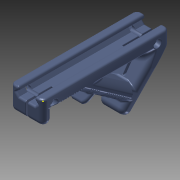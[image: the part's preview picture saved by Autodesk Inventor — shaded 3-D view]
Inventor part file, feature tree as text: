
AUTODESK INVENTOR PART (.ipt)
format: ipt  version: 2015 (Build 190159000, 159)  size: 5,217,280 bytes
history: native  units: mm
features: extrude x21, sketch x21, projected_geometry x20, fillet x18, plane x5, other x2, chamfer x2
ambient origin geometry x8: Origin, YZ Plane, XZ Plane, XY Plane, X Axis, Y Axis, Z Axis, Center Point
bodies: Solid1 (feature_tree)
feature tree (89):
  extrude  "Extrusion1"  Depth=35.0mm
  extrude  "Extrusion2"  Depth=10.0mm
  extrude  "Extrusion3"  Depth=12.0mm
  other  "Work Axis2"
  other  "Work Point2"
  plane  "Work Plane2"
  extrude  "Extrusion5"  Depth=12.0mm
  sketch  "Sketch9"  dims[d14=15.0mm d15=10.0mm d16=15.0mm d17=0.0mm]
  extrude  "Extrusion4"  TaperAngle=90.0deg  [1 undecoded]
  plane  "Work Plane3"
  plane  "Work Plane5"
  extrude  "Extrusion8"  Depth=10.0mm
  fillet  "Fillet3"  Radius=15.0mm
  extrude  "Extrusion9"  Depth=10.0mm
  fillet  "Fillet5"  Radius=130.0mm
  fillet  "Fillet6"  Radius=35.531179mm
  fillet  "Fillet7"  Radius=18.5mm
  fillet  "Fillet8"  Radius=18.5mm
  fillet  "Fillet9"  Radius=7.5mm
  extrude  "Extrusion10"  Depth=36.0mm TaperAngle=0.0deg
  fillet  "Fillet10"  Radius=35.75mm
  fillet  "Fillet11"  [1 undecoded]
  fillet  "Fillet12"  Radius=34.0mm
  plane  "Work Plane4"
  extrude  "Extrusion11"  Depth=5.0mm
  extrude  "Extrusion12"  Depth=13.5mm TaperAngle=0.0deg
  extrude  "Extrusion13"  Depth=5.0mm
  fillet  "Fillet13"  Radius=2.0mm
  fillet  "Fillet14"  Radius=2.0mm
  fillet  "Fillet15"  Radius=2.0mm
  extrude  "Extrusion14"  Depth=9.0mm
  extrude  "Extrusion15"  Depth=8.5mm
  extrude  "Extrusion16"  Depth=3.0mm
  fillet  "Fillet16"  [1 undecoded]
  extrude  "Extrusion17"  Depth=2.0mm
  extrude  "Extrusion18"  Depth=1.0mm
  plane  "Work Plane6"
  extrude  "Extrusion19"  Depth=110.0mm
  sketch  "Sketch27"  dims[d125=2.0mm d128=13.5mm d129=0.0mm]
  extrude  "Extrusion21"  Depth=13.5mm TaperAngle=0.0deg
  extrude  "Extrusion22"  Depth=5.0mm
  fillet  "Fillet17"  Radius=2.0mm
  fillet  "Fillet18"  Radius=8.0mm
  fillet  "Fillet19"  Radius=8.0mm
  extrude  "Extrusion23"  Depth=4.25mm
  extrude  "Extrusion24"  Depth=1.5mm
  fillet  "Fillet20"  Radius=0.5mm
  chamfer  "Chamfer3"  Distance=0.5mm
  chamfer  "Chamfer4"  Distance=25.0mm
  fillet  "Fillet22"  Radius=1.0mm
  sketch  "Sketch1"  dims[d0=135.0mm d1=35.0mm]
  sketch  "Sketch2"  dims[d2=10.0mm d3=0.0mm d4=10.0mm]
  projected_geometry  "Projected Loop1"
  sketch  "Sketch3"  dims[d5=15.0mm d6=0.0mm d7=12.0mm]
  projected_geometry  "Projected Loop2"
  sketch  "Sketch4"  dims[d10=9.599311mm d11=12.0mm]
  projected_geometry  "Projected Loop3"
  sketch  "Sketch5"  dims[d12=35.0mm d13=90.0deg]
  sketch  "Sketch12"  dims[d18=17.0mm d19=10.0mm d20=130.0mm d21=0.0mm d23=35.531179mm d24=18.5mm d25=18.5mm d26=7.5mm]
  projected_geometry  "Projected Loop11"
  sketch  "Sketch14"  dims[d27=7.5mm d28=36.0mm d29=0.0mm d30=35.75mm d31=0.0mm d32=-5.0mm d44=34.0mm d45=0.0mm]
  sketch  "Sketch18"  dims[d46=5.0mm d48=5.0mm]
  projected_geometry  "Projected Loop26"
  sketch  "Sketch19"  dims[d49=5.0mm d50=13.5mm d51=0.0mm]
  sketch  "Sketch20"  dims[d60=5.0mm d61=5.0mm d62=2.0mm d63=2.0mm d64=2.0mm]
  sketch  "Sketch21"  dims[d67=2.0mm d112=9.0mm]
  sketch  "Sketch22"  dims[d113=8.5mm d114=8.5mm]
  sketch  "Sketch23"  dims[d115=3.0mm d116=3.0mm d117=45.0deg]
  projected_geometry  "Projected Loop28"
  sketch  "Sketch24"  dims[d118=13.5mm d119=0.0mm d120=2.0mm]
  projected_geometry  "Projected Loop29"
  projected_geometry  "Projected Loop30"
  projected_geometry  "Projected Loop31"
  sketch  "Sketch25"  dims[d121=2.0mm d122=1.0mm]
  sketch  "Sketch26"  dims[d123=-17.5mm d124=110.0mm]
  projected_geometry  "Projected Loop32"
  projected_geometry  "Projected Loop33"
  projected_geometry  "Projected Loop34"
  projected_geometry  "Projected Loop35"
  sketch  "Sketch28"  dims[d131=5.0mm d132=5.0mm d133=2.0mm d134=8.0mm d135=8.0mm]
  projected_geometry  "Projected Loop36"
  sketch  "Sketch29"  dims[d136=5.0mm d137=0.0mm d138=4.25mm]
  sketch  "Sketch30"  dims[d139=5.0mm d140=0.0mm d141=0.5mm d142=0.5mm d143=0.5mm d144=25.0mm d145=1.0mm d146=1.0mm d147=55.0mm d148=0.0mm d149=4.0mm d150=4.0mm d151=15.0mm d152=0.0mm d153=1.0mm d154=5.0mm d155=5.0mm d156=5.0mm d157=0.0mm d158=2.5mm d160=1.0mm d161=1.5mm d163=1.0mm d164=1.0mm d165=1.5mm d166=1.0mm d167=1.0mm d168=1.5mm d169=1.0mm d170=1.0mm d171=1.5mm d172=1.0mm d173=1.0mm d174=1.5mm d175=1.0mm d176=1.0mm d177=1.5mm d178=1.0mm d179=1.0mm d180=1.5mm d181=1.0mm d182=1.0mm d183=1.5mm d184=1.0mm d185=1.0mm d186=1.5mm d187=1.0mm d188=1.0mm d189=1.5mm d190=1.0mm d191=1.0mm d192=1.5mm d193=1.0mm d194=1.0mm d195=1.5mm d196=1.0mm d197=1.0mm d198=1.5mm d199=1.0mm d200=1.0mm d201=1.5mm d202=1.0mm d203=1.0mm d204=1.5mm d205=1.0mm d206=1.0mm d207=1.5mm d208=1.0mm d209=1.0mm d210=1.5mm d211=1.0mm d212=6.5mm d213=0.0mm d214=1.5mm d215=50.75mm d216=0.0mm d217=1.0mm d218=1.5mm d219=1.0mm d220=90.0deg d221=1.5mm d222=1.0mm d223=1.5mm d224=1.0mm d225=1.0mm d226=1.0mm d227=1.5mm d228=1.0mm d229=1.5mm d230=1.0mm d231=1.0mm d232=1.0mm d233=1.5mm d234=1.0mm d235=1.5mm d236=1.0mm d237=1.0mm d238=1.0mm d239=1.5mm d240=1.0mm d241=1.5mm d242=1.0mm d243=1.0mm d244=1.0mm d245=1.5mm d246=1.0mm d247=1.5mm d248=1.0mm d249=1.0mm d250=1.0mm d251=1.5mm d252=1.0mm d253=1.5mm d254=1.0mm d255=1.0mm d256=1.0mm d257=1.5mm d258=1.0mm d259=1.5mm d260=1.0mm d261=1.0mm d262=1.0mm d263=1.5mm d264=1.0mm d265=1.5mm d266=1.0mm d267=1.0mm d268=1.0mm d269=1.5mm d270=1.0mm d271=1.5mm d272=1.0mm d273=1.0mm d274=1.0mm d275=1.5mm d276=1.0mm d277=1.5mm d278=1.0mm d279=1.0mm d280=1.0mm d281=1.5mm d282=1.0mm d283=1.5mm d284=1.0mm d285=7.5mm d286=0.0mm d287=1.5mm d290=3.75mm d291=0.0mm d292=25.5mm d293=0.0mm d294=25.5mm d295=0.0mm d296=4.25mm d297=0.5mm d298=2.25mm d299=0.0mm d300=0.5mm d301=0.5mm d302=4.25mm d303=0.0mm d304=5.0mm d305=0.0mm d306=0.5mm d307=0.0mm d308=0.2mm d309=2.0mm d310=45.0deg d311=0.2mm d312=2.0mm d313=45.0deg d315=1.5mm d316=1.5mm d317=1.5mm]
  projected_geometry  "Project Cut Edges1"
  projected_geometry  "Project Cut Edges2"
  projected_geometry  "Project Cut Edges3"
  projected_geometry  "Project Cut Edges4"
  projected_geometry  "Project Cut Edges5"
  projected_geometry  "Project Cut Edges6"
note: 3 required parameter values undecoded (feature->parameter linkage not recoverable at this tier; creation-order binding heuristic only, values carry confidence <= 0.55)
